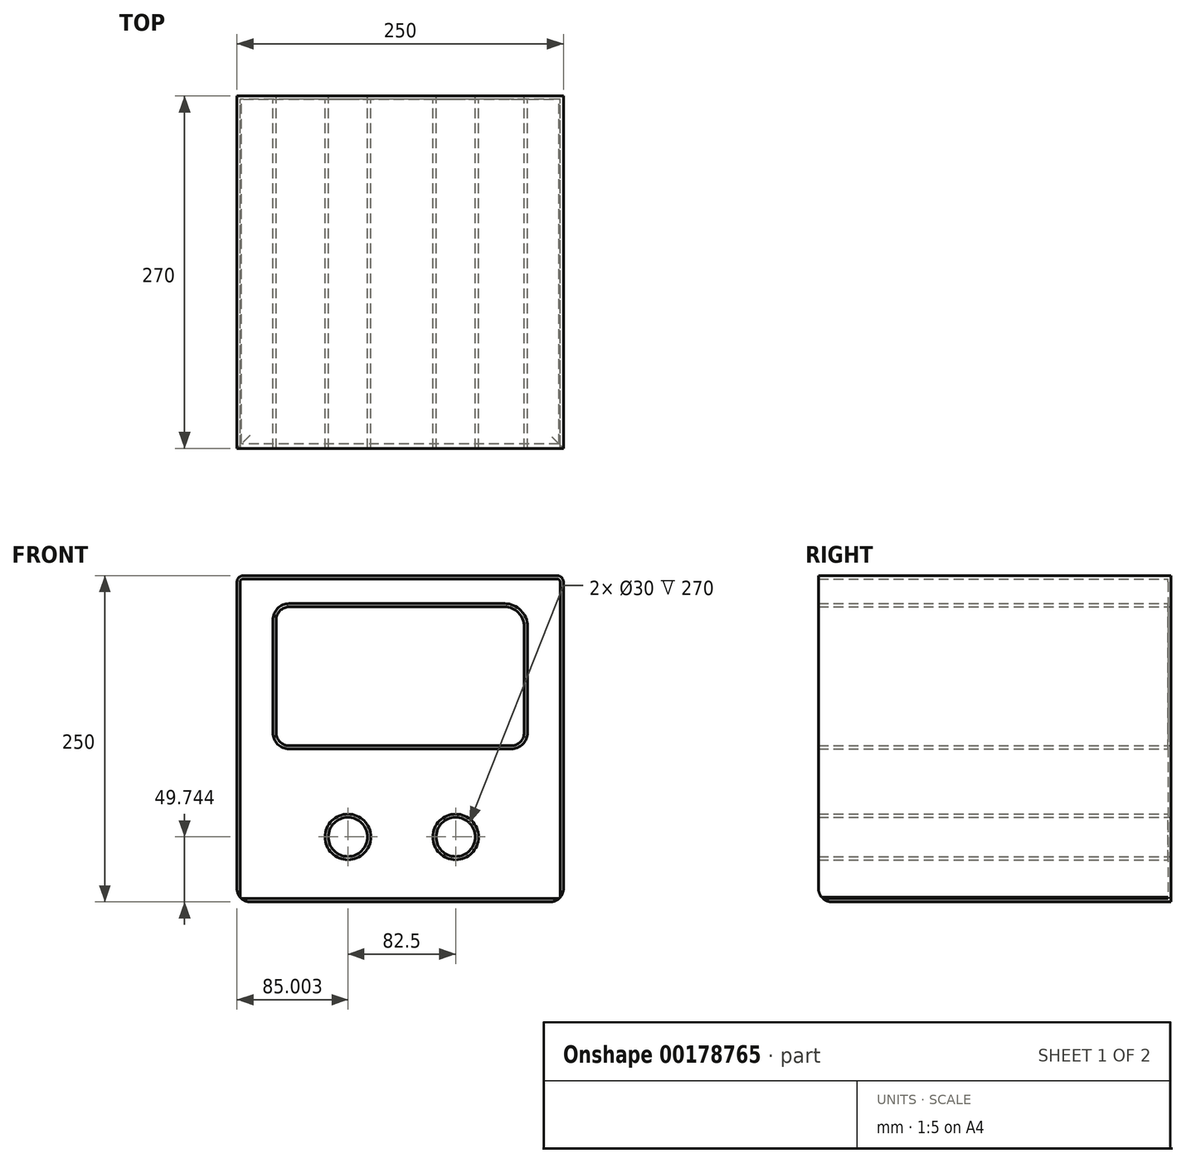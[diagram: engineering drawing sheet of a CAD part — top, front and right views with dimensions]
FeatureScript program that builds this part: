
annotation { "Feature Type Name" : "Feature", "Feature Type Description" : "" }
export const myFeature = defineFeature(function(context is Context, id is Id, definition is map)
    precondition{}
    {
        {
            var Q0;
            Q0=qCreatedBy(makeId("Front.planeOp"),FACE);
            var sketch = newSketch(context, id + "F0", { "sketchPlane" : qUnion([Q0])});
            skLineSegment(sketch, "E0", {"start": v(-45.29, 52.61) * mm, "end": v(204.71, 52.61) * mm});
            skLineSegment(sketch, "E1", {"start": v(204.71, 52.61) * mm, "end": v(204.71, -197.39) * mm});
            skLineSegment(sketch, "E2", {"start": v(204.71, -197.39) * mm, "end": v(-45.29, -197.39) * mm});
            skLineSegment(sketch, "E3", {"start": v(-45.29, -197.39) * mm, "end": v(-45.29, 52.61) * mm});
            skLineSegment(sketch, "E4", {"start": v(-15.29, 18.63) * mm, "end": v(-15.29, -67.73) * mm});
            skLineSegment(sketch, "E5", {"start": v(-5.27, -77.74) * mm, "end": v(164.7, -77.74) * mm});
            skLineSegment(sketch, "E6", {"start": v(174.71, -67.73) * mm, "end": v(174.71, 13.52) * mm});
            skLineSegment(sketch, "E7", {"start": v(159.6, 28.64) * mm, "end": v(-5.27, 28.64) * mm});
            skPoint(sketch, "E8.visualSharp", {"position": v(-15.29, 28.64) * mm});
            skArc(sketch, "E8.filletArc", {"start": v(-5.27, 28.64) * mm, "mid": v(-12.35, 25.7) * mm, "end": v(-15.29, 18.63) * mm});
            skPoint(sketch, "E9.visualSharp", {"position": v(174.71, 28.64) * mm});
            skArc(sketch, "E9.filletArc", {"start": v(174.71, 13.52) * mm, "mid": v(170.28, 24.21) * mm, "end": v(159.6, 28.64) * mm});
            skPoint(sketch, "E10.visualSharp", {"position": v(-15.29, -77.74) * mm});
            skArc(sketch, "E10.filletArc", {"start": v(-15.29, -67.73) * mm, "mid": v(-12.35, -74.8) * mm, "end": v(-5.27, -77.74) * mm});
            skPoint(sketch, "E11.visualSharp", {"position": v(174.71, -77.74) * mm});
            skArc(sketch, "E11.filletArc", {"start": v(164.7, -77.74) * mm, "mid": v(171.78, -74.8) * mm, "end": v(174.71, -67.73) * mm});
            skLineSegment(sketch, "E12", {"start": v(-45.29, -147.65) * mm, "end": v(39.71, -147.65) * mm, "construction": true});
            skLineSegment(sketch, "E13", {"start": v(39.71, -147.65) * mm, "end": v(204.71, -147.65) * mm, "construction": true});
            skLineSegment(sketch, "E14", {"start": v(204.71, -147.65) * mm, "end": v(122.21, -147.65) * mm, "construction": true});
            skCircle(sketch, "E15", {"center": v(39.71, -147.65) * mm, "radius": 15 * mm});
            skCircle(sketch, "E16", {"center": v(122.21, -147.65) * mm, "radius": 15 * mm});
            skSolve(sketch);
        }
        {
            var Q0;
            Q0=makeQuery(id+"F0.imprint","IMPRINT",FACE,{"disambiguationData":[TD([[makeQuery(id+"F0.imprint","IMPRINT",EDGE,{"derivedFrom":sQuery(id+"F0.wireOp",EDGE,"E0")}),-1.0]])]});
            extrude(context, id + "F1", {"entities" : qUnion([Q0]), "depth" : 20 * mm});
        }
        {
            var Q0;
            Q0=makeQuery(id+"F1.opExtrude","SWEPT_EDGE",EDGE,{"disambiguationData":[OSD([sQuery(id+"F0.wireOp",EDGE,"E0"),sQuery(id+"F0.wireOp",EDGE,"E1")])]});
            var Q1;
            Q1=makeQuery(id+"F1.opExtrude","SWEPT_EDGE",EDGE,{"disambiguationData":[OSD([sQuery(id+"F0.wireOp",EDGE,"E0"),sQuery(id+"F0.wireOp",EDGE,"E3")])]});
            fillet(context, id + "F2", {"entities" : qUnion([Q0, Q1]), "radius" : 5 * mm, "tangentPropagation" : true, "allowEdgeOverflow" : false});
        }
        {
            var Q0;
            Q0=makeQuery(id+"F1.opExtrude","CAP_FACE",FACE,{"disambiguationData":[OSD([sQuery(id+"F0.wireOp",EDGE,"E0"),sQuery(id+"F0.wireOp",EDGE,"E1"),sQuery(id+"F0.wireOp",EDGE,"E2"),sQuery(id+"F0.wireOp",EDGE,"E3"),sQuery(id+"F0.wireOp",EDGE,"E4"),sQuery(id+"F0.wireOp",EDGE,"E5"),sQuery(id+"F0.wireOp",EDGE,"E6"),sQuery(id+"F0.wireOp",EDGE,"E7"),sQuery(id+"F0.wireOp",EDGE,"E8.filletArc"),sQuery(id+"F0.wireOp",EDGE,"E9.filletArc"),sQuery(id+"F0.wireOp",EDGE,"E10.filletArc"),sQuery(id+"F0.wireOp",EDGE,"E11.filletArc"),sQuery(id+"F0.wireOp",EDGE,"E15"),sQuery(id+"F0.wireOp",EDGE,"E16")])],"isStart":false});
            var Q1;
            Q1=sQuery(id+"F0.wireOp",EDGE,"E15");
            extrude(context, id + "F3", {"entities" : qUnion([Q0]), "operationType" : NewBodyOperationType.ADD, "surfaceEntities" : qUnion([Q1]), "depth" : 250 * mm});
        }
        {
            var Q0;
            Q0=sQuery(id+"F0.wireOp",EDGE,"E16");
            var Q1;
            Q1=sQuery(id+"F0.wireOp",EDGE,"E15");
            extrude(context, id + "F4", {"bodyType" : ToolBodyType.SURFACE, "surfaceEntities" : qUnion([Q0, Q1]), "depth" : 351 * mm});
        }
        {
            var Q0;
            Q0=makeQuery(id+"F3.opExtrude","CAP_FACE",FACE,{"disambiguationData":[OSD([sQuery(id+"F0.wireOp",EDGE,"E0"),sQuery(id+"F0.wireOp",EDGE,"E1"),sQuery(id+"F0.wireOp",EDGE,"E2"),sQuery(id+"F0.wireOp",EDGE,"E3"),sQuery(id+"F0.wireOp",EDGE,"E4"),sQuery(id+"F0.wireOp",EDGE,"E5"),sQuery(id+"F0.wireOp",EDGE,"E6"),sQuery(id+"F0.wireOp",EDGE,"E7"),sQuery(id+"F0.wireOp",EDGE,"E8.filletArc"),sQuery(id+"F0.wireOp",EDGE,"E9.filletArc"),sQuery(id+"F0.wireOp",EDGE,"E10.filletArc"),sQuery(id+"F0.wireOp",EDGE,"E11.filletArc"),sQuery(id+"F0.wireOp",EDGE,"E15"),sQuery(id+"F0.wireOp",EDGE,"E16")])],"isStart":false});
            shell(context, id + "F5", {"entities" : qUnion([Q0]), "thickness" : 2.5 * mm});
        }
        {
            var Q0;
            {var subQ0=sQuery(id+"F0.wireOp",EDGE,"E2");var subQ1=sQuery(id+"F0.wireOp",EDGE,"E1");Q0=makeQuery(id+"F3.boolean.opBoolean","MERGE",EDGE,{"derivedFrom":[makeQuery(id+"F1.opExtrude","SWEPT_EDGE",EDGE,{"disambiguationData":[OSD([subQ1,subQ0])]}),makeQuery(id+"F3.opExtrude","SWEPT_EDGE",EDGE,{"disambiguationData":[OSD([subQ1,subQ0])]})]});}
            var Q1;
            {var subQ0=sQuery(id+"F0.wireOp",EDGE,"E3");var subQ1=sQuery(id+"F0.wireOp",EDGE,"E2");Q1=makeQuery(id+"F3.boolean.opBoolean","MERGE",EDGE,{"derivedFrom":[makeQuery(id+"F1.opExtrude","SWEPT_EDGE",EDGE,{"disambiguationData":[OSD([subQ1,subQ0])]}),makeQuery(id+"F3.opExtrude","SWEPT_EDGE",EDGE,{"disambiguationData":[OSD([subQ1,subQ0])]})]});}
            var Q2;
            Q2=makeQuery(id+"F3.opExtrude","CAP_EDGE",EDGE,{"disambiguationData":[OSD([sQuery(id+"F0.wireOp",EDGE,"E2")])],"isStart":false});
            fillet(context, id + "F6", {"entities" : qUnion([Q0, Q1, Q2]), "radius" : 10 * mm, "tangentPropagation" : true, "allowEdgeOverflow" : false});
        }
    });
